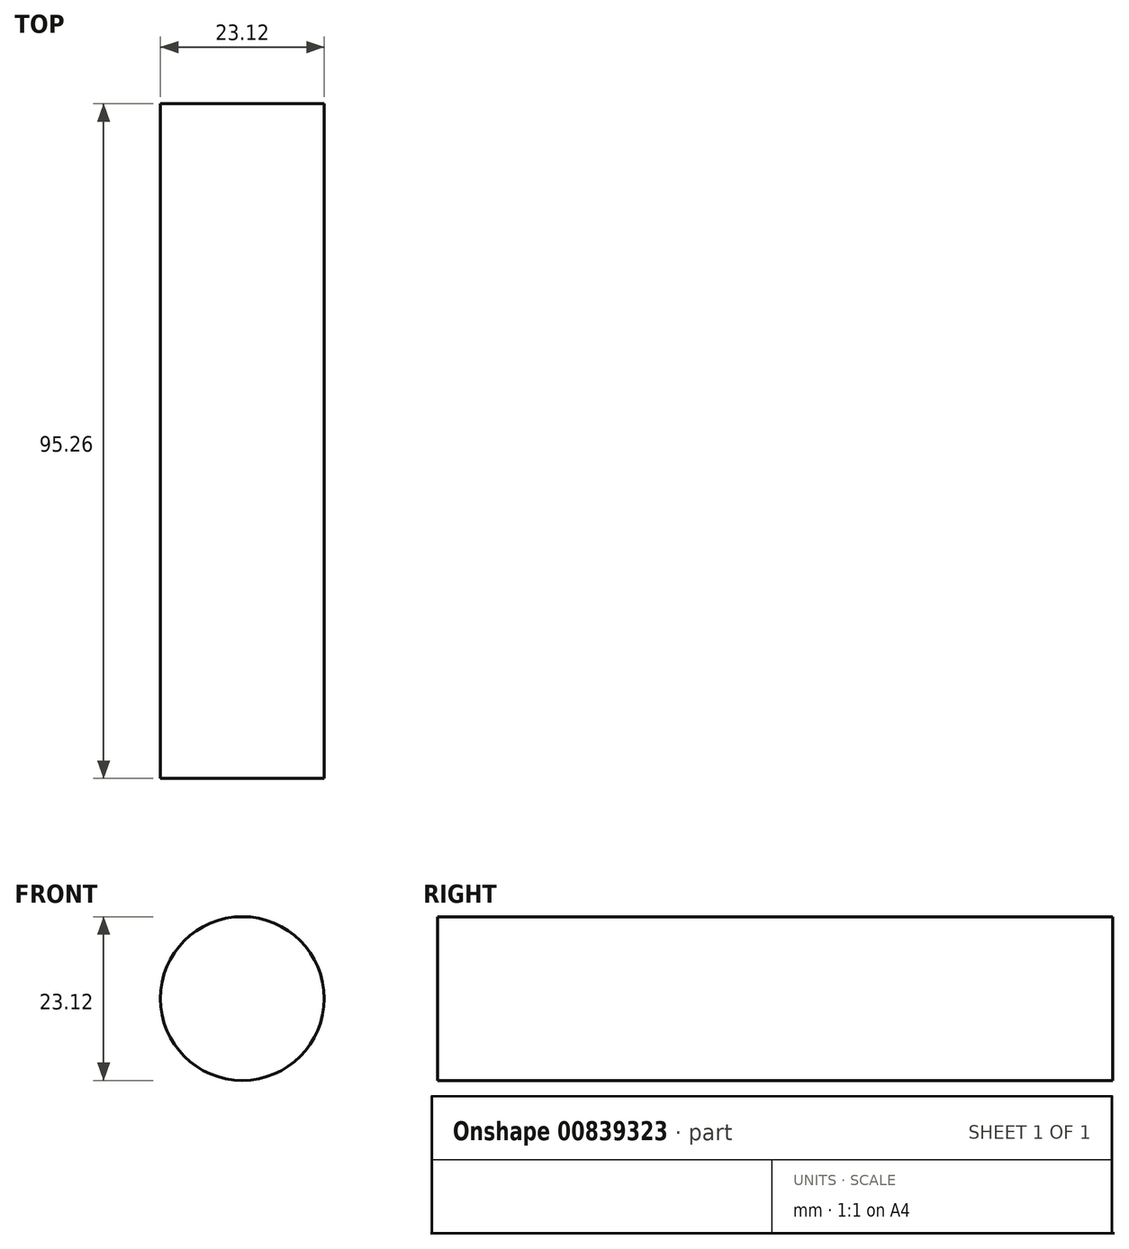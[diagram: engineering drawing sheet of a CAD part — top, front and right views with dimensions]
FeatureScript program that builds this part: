
annotation { "Feature Type Name" : "Feature", "Feature Type Description" : "" }
export const myFeature = defineFeature(function(context is Context, id is Id, definition is map)
    precondition{}
    {
        {
            var Q0;
            Q0=qCreatedBy(makeId("Front.planeOp"),FACE);
            var sketch = newSketch(context, id + "F0", { "sketchPlane" : qUnion([Q0])});
            skCircle(sketch, "E0", {"center": v(0, 0) * mm, "radius": 11.56 * mm});
            skSolve(sketch);
        }
        {
            var Q0;
            Q0 = qSketchRegion(id + "F0", true);
            extrude(context, id + "F1", {"entities" : qUnion([Q0]), "depth" : 47.62 * mm, "offsetDistance" : 25.4 * mm, "hasSecondDirection" : true, "secondDirectionOppositeDirection" : true, "secondDirectionDepth" : 47.62 * mm});
        }
    });
